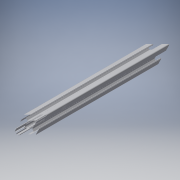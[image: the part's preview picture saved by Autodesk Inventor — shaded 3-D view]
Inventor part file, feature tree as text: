
AUTODESK INVENTOR PART (.ipt)
format: ipt  version: 2016 (Build 200138000, 138)  size: 310,272 bytes
history: native  units: in
note: dims shown in document units (in); Inventor stores cm internally (conversion verified against a paired STEP export)
features: other x3, extrude x1, sketch x1
ambient origin geometry x8: Origin, YZ Plane, XZ Plane, XY Plane, X Axis, Y Axis, Z Axis, Center Point
bodies: Solid1 (feature_tree)
feature tree (5):
  other  "Blocks"
  extrude  "Extrusion1"  [1 undecoded]
  sketch  "Sketch1"  dims[d1=0.0in]
  other  "20x20"
  other  "20x20:1"
note: 1 required parameter value undecoded (feature->parameter linkage not recoverable at this tier; creation-order binding heuristic only, values carry confidence <= 0.55)
